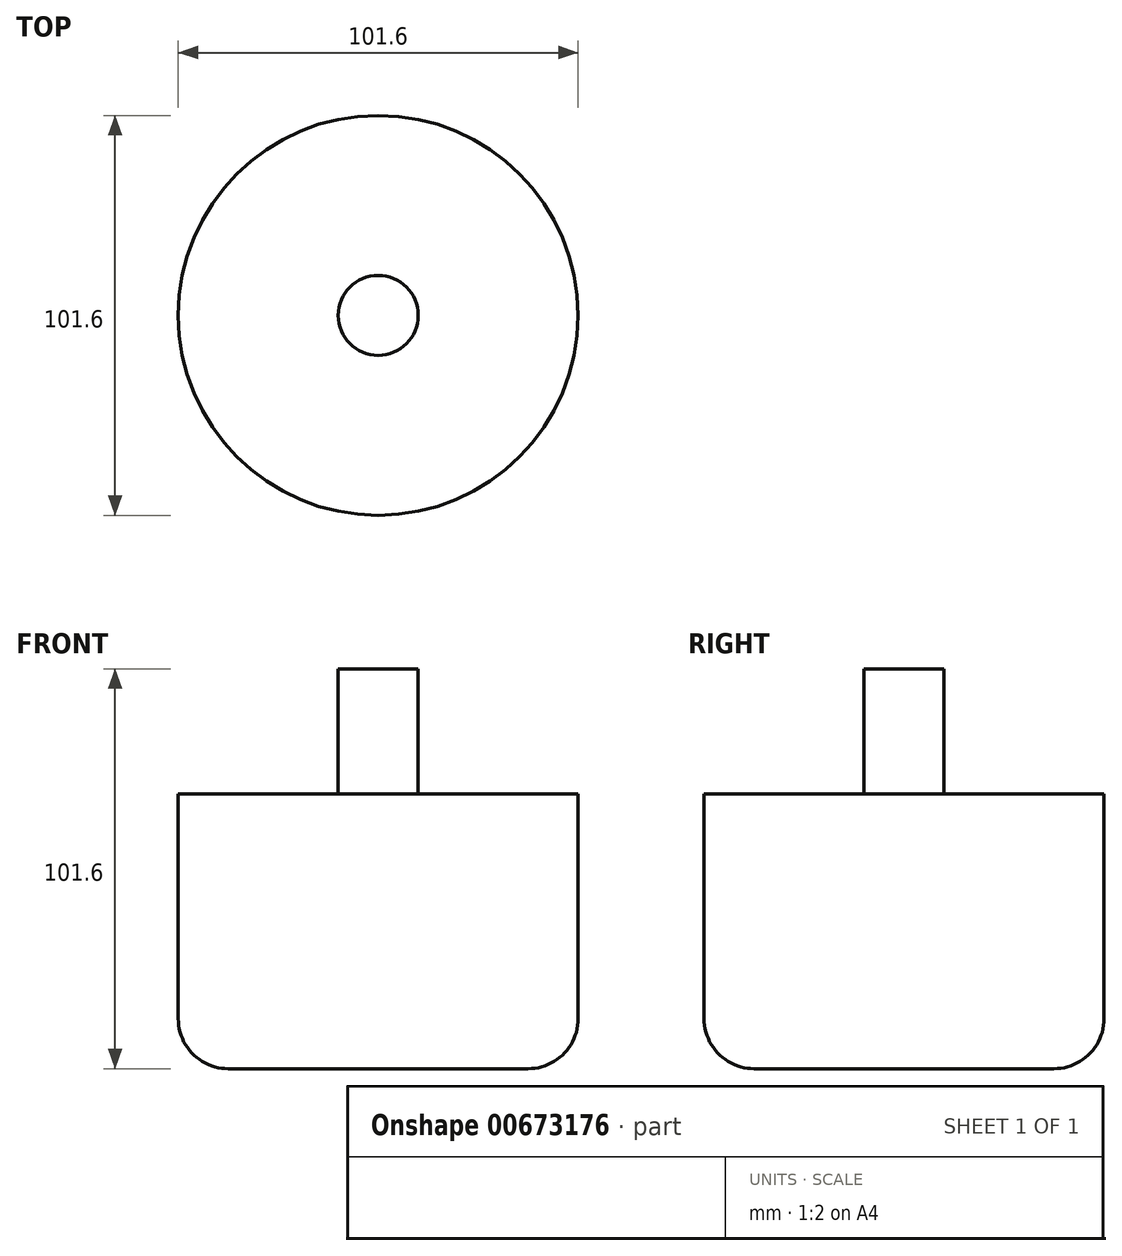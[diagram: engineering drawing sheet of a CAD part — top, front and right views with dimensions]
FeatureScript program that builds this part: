
annotation { "Feature Type Name" : "Feature", "Feature Type Description" : "" }
export const myFeature = defineFeature(function(context is Context, id is Id, definition is map)
    precondition{}
    {
        {
            var Q0;
            Q0=qCreatedBy(makeId("Top.planeOp"),FACE);
            var sketch = newSketch(context, id + "F0", { "sketchPlane" : qUnion([Q0])});
            skCircle(sketch, "E0", {"center": v(0, 0) * mm, "radius": 50.8 * mm});
            skSolve(sketch);
        }
        {
            var Q0;
            Q0 = qSketchRegion(id + "F0", true);
            extrude(context, id + "F1", {"entities" : qUnion([Q0]), "depth" : 69.85 * mm, "offsetDistance" : 25.4 * mm});
        }
        {
            var Q0;
            Q0=makeQuery(id+"F1.opExtrude","CAP_FACE",FACE,{"disambiguationData":[OSD([sQuery(id+"F0.wireOp",EDGE,"E0")])],"isStart":false});
            var sketch = newSketch(context, id + "F2", { "sketchPlane" : qUnion([Q0])});
            skCircle(sketch, "E1", {"center": v(0, 0) * mm, "radius": 10.16 * mm});
            skSolve(sketch);
        }
        {
            var Q0;
            Q0 = qSketchRegion(id + "F2", true);
            extrude(context, id + "F3", {"entities" : qUnion([Q0]), "operationType" : NewBodyOperationType.ADD, "depth" : 31.75 * mm, "offsetDistance" : 25.4 * mm});
        }
        {
            var Q0;
            Q0=makeQuery(id+"F1.opExtrude","CAP_EDGE",EDGE,{"disambiguationData":[OSD([sQuery(id+"F0.wireOp",EDGE,"E0")])],"isStart":true});
            fillet(context, id + "F4", {"entities" : qUnion([Q0]), "radius" : 12.7 * mm, "tangentPropagation" : true, "allowEdgeOverflow" : false});
        }
    });
